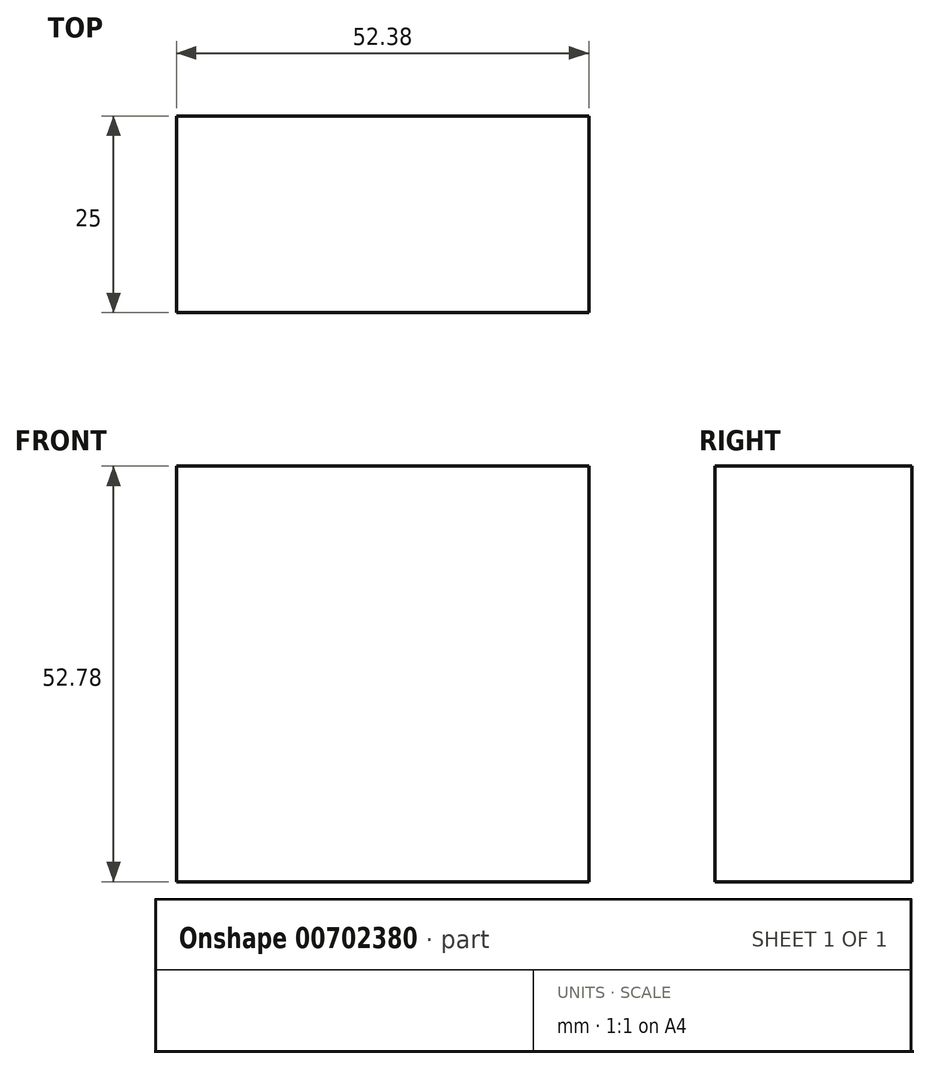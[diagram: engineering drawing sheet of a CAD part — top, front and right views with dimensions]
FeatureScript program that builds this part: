
annotation { "Feature Type Name" : "Feature", "Feature Type Description" : "" }
export const myFeature = defineFeature(function(context is Context, id is Id, definition is map)
    precondition{}
    {
        {
            var Q0;
            Q0=qCreatedBy(makeId("Front.planeOp"),FACE);
            var sketch = newSketch(context, id + "F0", { "sketchPlane" : qUnion([Q0])});
            skLineSegment(sketch, "E0.bottom", {"start": v(-62.7, -23.98) * mm, "end": v(-10.33, -23.98) * mm});
            skLineSegment(sketch, "E0.top", {"start": v(-62.7, 28.8) * mm, "end": v(-10.33, 28.8) * mm});
            skLineSegment(sketch, "E0.left", {"start": v(-62.7, -23.98) * mm, "end": v(-62.7, 28.8) * mm});
            skLineSegment(sketch, "E0.right", {"start": v(-10.33, -23.98) * mm, "end": v(-10.33, 28.8) * mm});
            skSolve(sketch);
        }
        {
            var Q0;
            Q0 = qSketchRegion(id + "F0", true);
            extrude(context, id + "F1", {"entities" : qUnion([Q0]), "depth" : 25 * mm, "offsetDistance" : 25 * mm});
        }
    });
